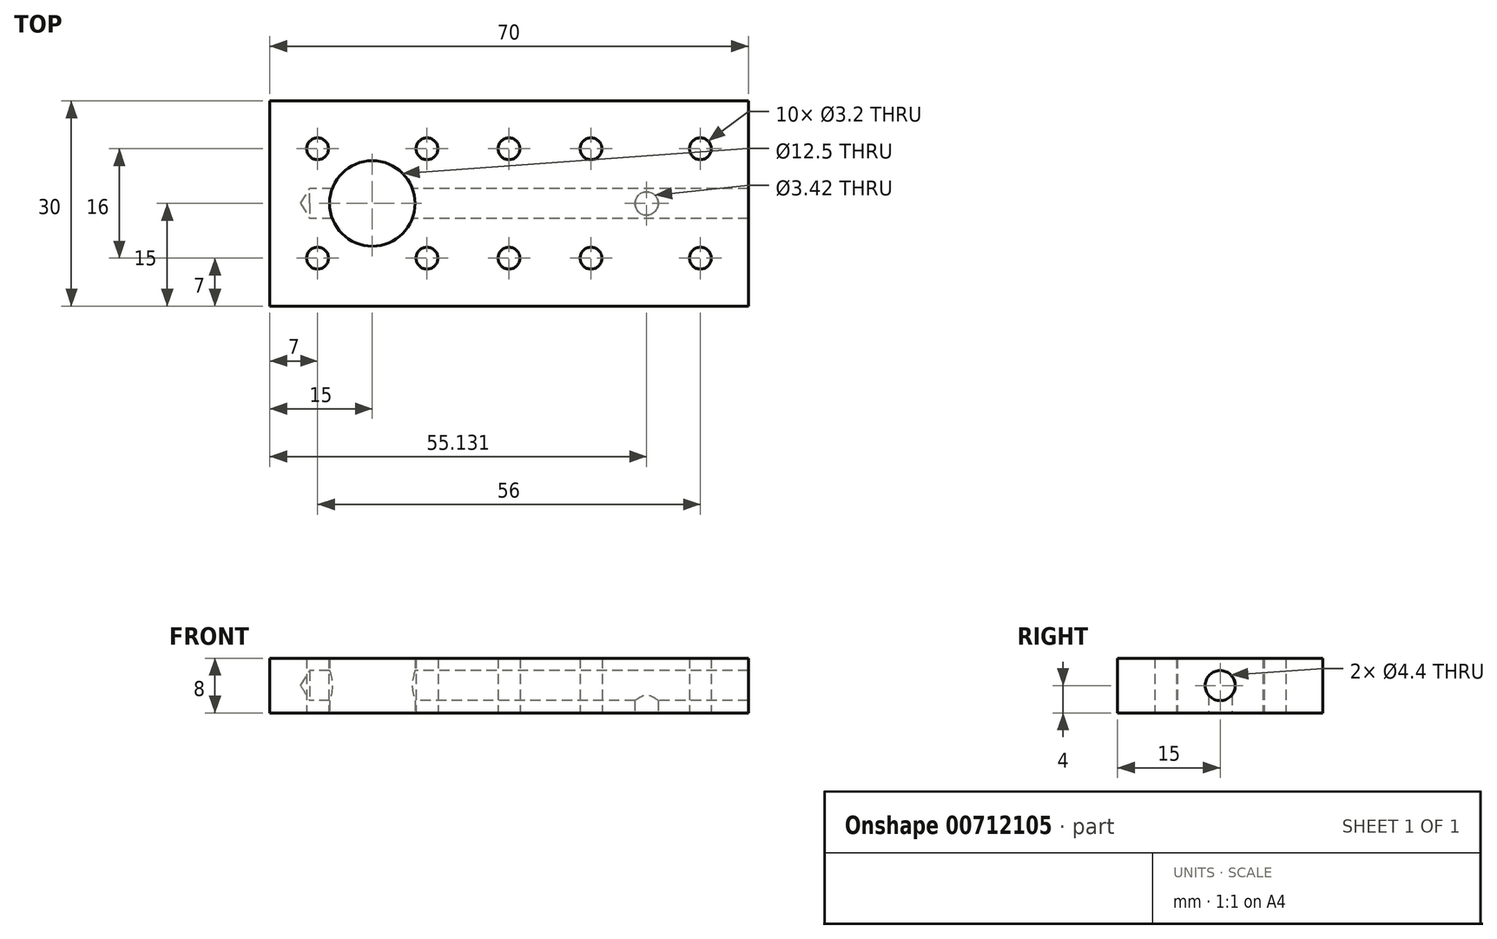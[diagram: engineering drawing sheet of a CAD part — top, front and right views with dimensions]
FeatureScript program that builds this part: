
annotation { "Feature Type Name" : "Feature", "Feature Type Description" : "" }
export const myFeature = defineFeature(function(context is Context, id is Id, definition is map)
    precondition{}
    {
        {
            var Q0;
            Q0=qCreatedBy(makeId("Top.planeOp"),FACE);
            var sketch = newSketch(context, id + "F0", { "sketchPlane" : qUnion([Q0])});
            skLineSegment(sketch, "E0.bottom", {"start": v(35, -15) * mm, "end": v(-35, -15) * mm});
            skLineSegment(sketch, "E0.top", {"start": v(35, 15) * mm, "end": v(-35, 15) * mm});
            skLineSegment(sketch, "E0.left", {"start": v(35, -15) * mm, "end": v(35, 15) * mm});
            skLineSegment(sketch, "E0.right", {"start": v(-35, -15) * mm, "end": v(-35, 15) * mm});
            skPoint(sketch, "E0.middle", {"position": v(0, 0) * mm});
            skLineSegment(sketch, "E1", {"start": v(44.4, 0) * mm, "end": v(-41.76, 0) * mm, "construction": true});
            skLineSegment(sketch, "E2", {"start": v(0, 28.57) * mm, "end": v(0, -25.3) * mm, "construction": true});
            skLineSegment(sketch, "E3.0", {"start": v(-20, 28.57) * mm, "end": v(-20, -25.3) * mm, "construction": true});
            skLineSegment(sketch, "E4.0", {"start": v(-28, 28.57) * mm, "end": v(-28, -25.3) * mm, "construction": true});
            skLineSegment(sketch, "E5.0", {"start": v(-12, 28.57) * mm, "end": v(-12, -25.3) * mm, "construction": true});
            skLineSegment(sketch, "E6.MirrorCS", {"start": v(28, 28.57) * mm, "end": v(28, -25.3) * mm, "construction": true});
            skLineSegment(sketch, "E7.MirrorCS", {"start": v(12, 28.57) * mm, "end": v(12, -25.3) * mm, "construction": true});
            skLineSegment(sketch, "E8.MirrorCS", {"start": v(20, 28.57) * mm, "end": v(20, -25.3) * mm, "construction": true});
            skLineSegment(sketch, "E9.0", {"start": v(44.4, 8) * mm, "end": v(-41.76, 8) * mm, "construction": true});
            skLineSegment(sketch, "E10.0", {"start": v(44.4, -8) * mm, "end": v(-41.76, -8) * mm, "construction": true});
            skPoint(sketch, "E11", {"position": v(28, 8) * mm});
            skPoint(sketch, "E12", {"position": v(12, 8) * mm});
            skPoint(sketch, "E13", {"position": v(20, 0) * mm});
            skPoint(sketch, "E14", {"position": v(28, -8) * mm});
            skPoint(sketch, "E15", {"position": v(12, -8) * mm});
            skPoint(sketch, "E16", {"position": v(0, 8) * mm});
            skPoint(sketch, "E17", {"position": v(0, -8) * mm});
            skPoint(sketch, "E18", {"position": v(-12, 8) * mm});
            skPoint(sketch, "E19", {"position": v(-12, -8) * mm});
            skPoint(sketch, "E20", {"position": v(-28, -8) * mm});
            skPoint(sketch, "E21", {"position": v(-28, 8) * mm});
            skPoint(sketch, "E22", {"position": v(-20, 0) * mm});
            skSolve(sketch);
        }
        {
            var Q0;
            Q0=makeQuery(id+"F0.imprint","IMPRINT",FACE,{"disambiguationData":[TD([[makeQuery(id+"F0.imprint","IMPRINT",EDGE,{"derivedFrom":sQuery(id+"F0.wireOp",EDGE,"E0.bottom")}),-1.0]])]});
            extrude(context, id + "F1", {"entities" : qUnion([Q0]), "oppositeDirection" : true, "depth" : 8 * mm, "offsetDistance" : 25 * mm});
        }
        {
            var Q0;
            Q0=sQuery(id+"F0.wireOp",VERTEX,"E21");
            var Q1;
            Q1=sQuery(id+"F0.wireOp",VERTEX,"E18");
            var Q2;
            Q2=sQuery(id+"F0.wireOp",VERTEX,"E20");
            var Q3;
            Q3=sQuery(id+"F0.wireOp",VERTEX,"E19");
            var Q4;
            Q4=sQuery(id+"F0.wireOp",VERTEX,"E16");
            var Q5;
            Q5=sQuery(id+"F0.wireOp",VERTEX,"E17");
            var Q6;
            Q6=sQuery(id+"F0.wireOp",VERTEX,"E12");
            var Q7;
            Q7=sQuery(id+"F0.wireOp",VERTEX,"E15");
            var Q8;
            Q8=sQuery(id+"F0.wireOp",VERTEX,"E11");
            var Q9;
            Q9=sQuery(id+"F0.wireOp",VERTEX,"E14");
            var Q10;
            Q10=makeQuery(id+"F1.opExtrude","SWEPT_BODY",BODY,{"disambiguationData":[OSD([sQuery(id+"F0.wireOp",EDGE,"E0.bottom"),sQuery(id+"F0.wireOp",EDGE,"E0.top"),sQuery(id+"F0.wireOp",EDGE,"E0.left"),sQuery(id+"F0.wireOp",EDGE,"E0.right")])]});
            hole(context, id + "F2", {"style" : HoleStyle.SIMPLE, "endStyle" : HoleEndStyle.THROUGH, "holeDiameter" : 3.2 * mm, "majorDiameter" : 5 * mm, "tappedDepth" : 12 * mm, "tapClearance" : 3, "locations" : qUnion([Q0, Q1, Q2, Q3, Q4, Q5, Q6, Q7, Q8, Q9]), "scope" : qUnion([Q10]), "startStyle" : HoleStartStyle.PART});
        }
        {
            var Q0;
            Q0=sQuery(id+"F0.wireOp",VERTEX,"E22");
            var Q1;
            Q1=makeQuery(id+"F1.opExtrude","SWEPT_BODY",BODY,{"disambiguationData":[OSD([sQuery(id+"F0.wireOp",EDGE,"E0.bottom"),sQuery(id+"F0.wireOp",EDGE,"E0.top"),sQuery(id+"F0.wireOp",EDGE,"E0.left"),sQuery(id+"F0.wireOp",EDGE,"E0.right")])]});
            hole(context, id + "F3", {"style" : HoleStyle.SIMPLE, "endStyle" : HoleEndStyle.THROUGH, "holeDiameter" : 12.5 * mm, "majorDiameter" : 5 * mm, "tappedDepth" : 12 * mm, "tapClearance" : 3, "locations" : qUnion([Q0]), "scope" : qUnion([Q1]), "startStyle" : HoleStartStyle.PART});
        }
        {
            var Q0;
            Q0=makeQuery(id+"F1.opExtrude","SWEPT_FACE",FACE,{"disambiguationData":[OSD([sQuery(id+"F0.wireOp",EDGE,"E0.left")])]});
            var sketch = newSketch(context, id + "F4", { "sketchPlane" : qUnion([Q0])});
            skLineSegment(sketch, "E23", {"start": v(-15, -4) * mm, "end": v(15, -4) * mm, "construction": true});
            skPoint(sketch, "E24", {"position": v(0, -4) * mm});
            skSolve(sketch);
        }
        {
            var Q0;
            Q0=sQuery(id+"F4.wireOp",VERTEX,"E24");
            var Q1;
            Q1=makeQuery(id+"F1.opExtrude","SWEPT_BODY",BODY,{"disambiguationData":[OSD([sQuery(id+"F0.wireOp",EDGE,"E0.bottom"),sQuery(id+"F0.wireOp",EDGE,"E0.top"),sQuery(id+"F0.wireOp",EDGE,"E0.left"),sQuery(id+"F0.wireOp",EDGE,"E0.right")])]});
            hole(context, id + "F5", {"style" : HoleStyle.SIMPLE, "endStyle" : HoleEndStyle.BLIND, "holeDiameter" : 3.5 * mm, "majorDiameter" : 5 * mm, "holeDepth" : 50 * mm, "tappedDepth" : 12 * mm, "tapClearance" : 3, "locations" : qUnion([Q0]), "scope" : qUnion([Q1]), "startStyle" : HoleStartStyle.PART});
        }
        {
            var Q0;
            Q0=sQuery(id+"F4.wireOp",VERTEX,"E24");
            var Q1;
            Q1=makeQuery(id+"F1.opExtrude","SWEPT_BODY",BODY,{"disambiguationData":[OSD([sQuery(id+"F0.wireOp",EDGE,"E0.bottom"),sQuery(id+"F0.wireOp",EDGE,"E0.top"),sQuery(id+"F0.wireOp",EDGE,"E0.left"),sQuery(id+"F0.wireOp",EDGE,"E0.right")])]});
            hole(context, id + "F6", {"style" : HoleStyle.SIMPLE, "endStyle" : HoleEndStyle.BLIND, "standardTappedOrClearance" : lookupTablePath({ "standard" : "ISO", "fit" : "Normal", "size" : "M4", "type" : "Clearance" }), "standardBlindInLast" : lookupTablePath({ "fit" : "Standard", "standard" : "ISO", "size" : "M4", "type" : "Clearance" }), "holeDiameter" : 4.4 * mm, "majorDiameter" : 5 * mm, "holeDepth" : 15 * mm, "tappedDepth" : 12 * mm, "tapClearance" : 3, "locations" : qUnion([Q0]), "scope" : qUnion([Q1]), "startStyle" : HoleStartStyle.PART});
        }
        {
            var Q0;
            Q0=makeQuery(id+"F1.opExtrude","CAP_FACE",FACE,{"disambiguationData":[OSD([sQuery(id+"F0.wireOp",EDGE,"E0.bottom"),sQuery(id+"F0.wireOp",EDGE,"E0.top"),sQuery(id+"F0.wireOp",EDGE,"E0.left"),sQuery(id+"F0.wireOp",EDGE,"E0.right")])],"isStart":false});
            var sketch = newSketch(context, id + "F7", { "sketchPlane" : qUnion([Q0])});
            skCircle(sketch, "E25", {"center": v(20.13, 0) * mm, "radius": 1.71 * mm});
            skSolve(sketch);
        }
        {
            var Q0;
            Q0=makeQuery(id+"F7.imprint","IMPRINT",FACE,{"disambiguationData":[TD([[makeQuery(id+"F7.imprint","IMPRINT",EDGE,{"derivedFrom":sQuery(id+"F7.wireOp",EDGE,"E25")}),1.0]])]});
            extrude(context, id + "F8", {"entities" : qUnion([Q0]), "operationType" : NewBodyOperationType.REMOVE, "endBound" : BoundingType.UP_TO_NEXT, "oppositeDirection" : true, "depth" : 25 * mm, "offsetDistance" : 25 * mm});
        }
    });
